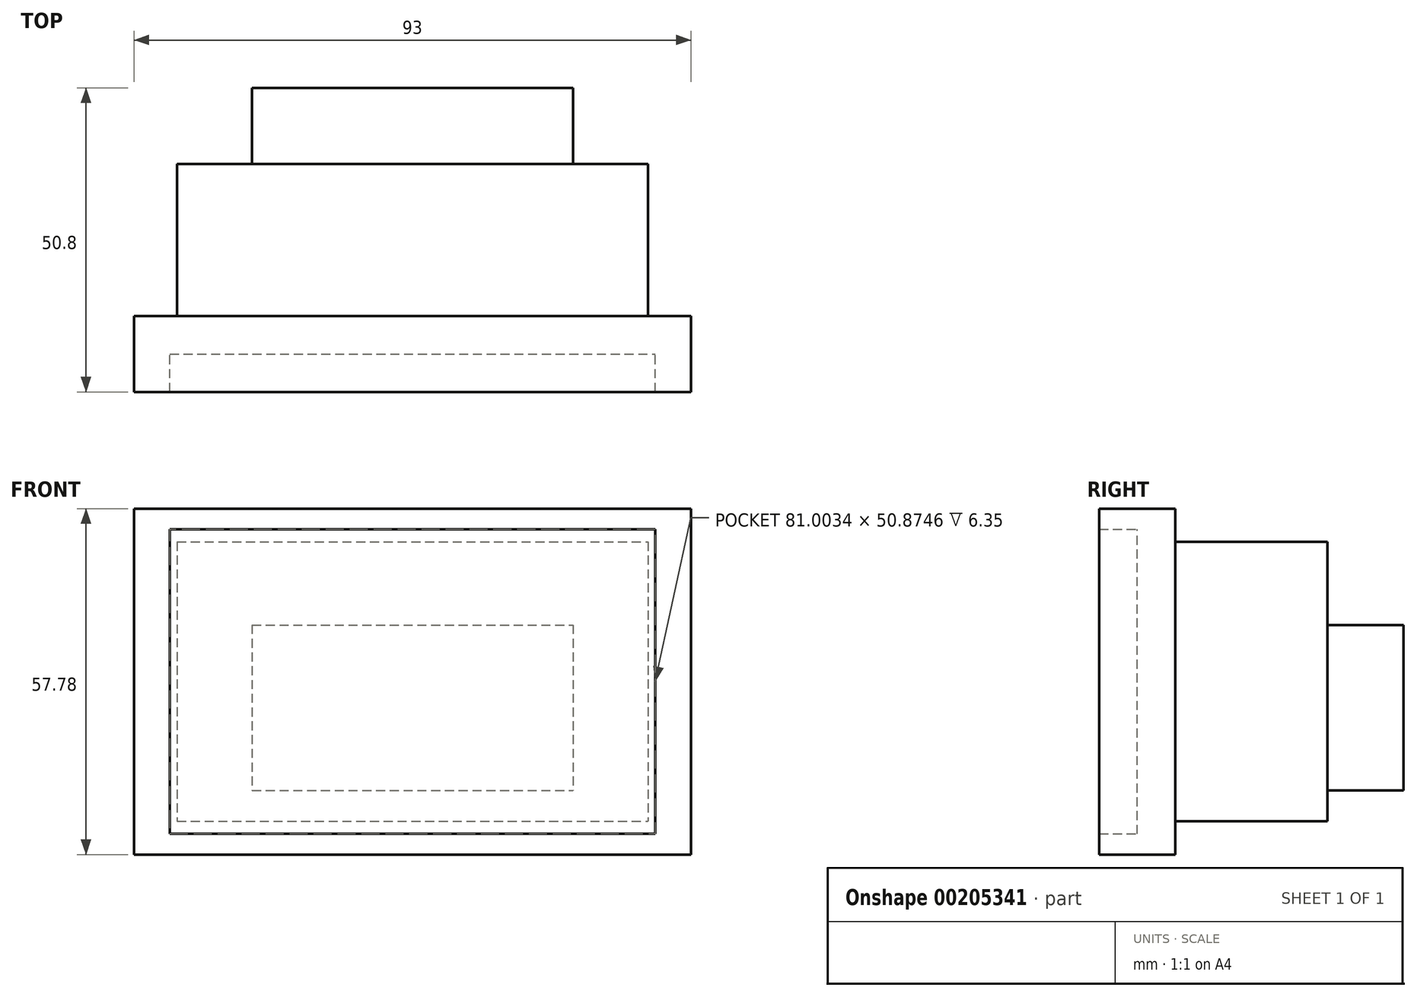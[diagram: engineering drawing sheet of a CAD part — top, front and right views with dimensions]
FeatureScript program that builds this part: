
annotation { "Feature Type Name" : "Feature", "Feature Type Description" : "" }
export const myFeature = defineFeature(function(context is Context, id is Id, definition is map)
    precondition{}
    {
        {
            var Q0;
            Q0=qCreatedBy(makeId("Front.planeOp"),FACE);
            var sketch = newSketch(context, id + "F0", { "sketchPlane" : qUnion([Q0])});
            skLineSegment(sketch, "E0.bottom", {"start": v(44.23, 29.1) * mm, "end": v(-44.23, 29.1) * mm});
            skLineSegment(sketch, "E0.top", {"start": v(44.23, -29.1) * mm, "end": v(-44.23, -29.1) * mm});
            skLineSegment(sketch, "E0.left", {"start": v(44.23, 29.1) * mm, "end": v(44.23, -29.1) * mm});
            skLineSegment(sketch, "E0.right", {"start": v(-44.23, 29.1) * mm, "end": v(-44.23, -29.1) * mm});
            skPoint(sketch, "E0.middle", {"position": v(0, 0) * mm});
            skLineSegment(sketch, "E1.bottom", {"start": v(40.81, 25.7) * mm, "end": v(-40.81, 25.7) * mm});
            skLineSegment(sketch, "E1.top", {"start": v(40.81, -25.7) * mm, "end": v(-40.81, -25.7) * mm});
            skLineSegment(sketch, "E1.left", {"start": v(40.81, 25.7) * mm, "end": v(40.81, -25.7) * mm});
            skLineSegment(sketch, "E1.right", {"start": v(-40.81, 25.7) * mm, "end": v(-40.81, -25.7) * mm});
            skSolve(sketch);
        }
        {
            var Q0;
            Q0=makeQuery(id+"F0.imprint","IMPRINT",FACE,{"disambiguationData":[TD([[makeQuery(id+"F0.imprint","IMPRINT",EDGE,{"derivedFrom":sQuery(id+"F0.wireOp",EDGE,"E1.bottom")}),1.0]])]});
            extrude(context, id + "F1", {"entities" : qUnion([Q0]), "depth" : 6.35 * mm});
        }
        {
            var Q0;
            Q0=qCreatedBy(makeId("Front.planeOp"),FACE);
            var sketch = newSketch(context, id + "F2", { "sketchPlane" : qUnion([Q0])});
            skLineSegment(sketch, "E2.bottom", {"start": v(46.5, 28.89) * mm, "end": v(-46.5, 28.89) * mm});
            skLineSegment(sketch, "E2.top", {"start": v(46.5, -28.89) * mm, "end": v(-46.5, -28.89) * mm});
            skLineSegment(sketch, "E2.left", {"start": v(46.5, 28.89) * mm, "end": v(46.5, -28.89) * mm});
            skLineSegment(sketch, "E2.right", {"start": v(-46.5, 28.89) * mm, "end": v(-46.5, -28.89) * mm});
            skPoint(sketch, "E2.middle", {"position": v(0, 0) * mm});
            skLineSegment(sketch, "E3.bottom", {"start": v(40.5, 25.44) * mm, "end": v(-40.5, 25.44) * mm});
            skLineSegment(sketch, "E3.top", {"start": v(40.5, -25.44) * mm, "end": v(-40.5, -25.44) * mm});
            skLineSegment(sketch, "E3.left", {"start": v(40.5, 25.44) * mm, "end": v(40.5, -25.44) * mm});
            skLineSegment(sketch, "E3.right", {"start": v(-40.5, 25.44) * mm, "end": v(-40.5, -25.44) * mm});
            skSolve(sketch);
        }
        {
            var Q0;
            Q0=makeQuery(id+"F2.imprint","IMPRINT",FACE,{"disambiguationData":[TD([[makeQuery(id+"F2.imprint","IMPRINT",EDGE,{"derivedFrom":sQuery(id+"F2.wireOp",EDGE,"E2.bottom")}),1.0]])]});
            extrude(context, id + "F3", {"entities" : qUnion([Q0]), "operationType" : NewBodyOperationType.ADD, "depth" : 12.7 * mm});
        }
        {
            var Q0;
            Q0=makeQuery(id+"F3.boolean.opBoolean","MERGE",FACE,{"derivedFrom":[makeQuery(id+"F1.opExtrude","CAP_FACE",FACE,{"disambiguationData":[OSD([sQuery(id+"F0.wireOp",EDGE,"E1.bottom"),sQuery(id+"F0.wireOp",EDGE,"E1.top"),sQuery(id+"F0.wireOp",EDGE,"E1.left"),sQuery(id+"F0.wireOp",EDGE,"E1.right")])],"isStart":true}),makeQuery(id+"F3.opExtrude","CAP_FACE",FACE,{"disambiguationData":[OSD([sQuery(id+"F2.wireOp",EDGE,"E2.bottom"),sQuery(id+"F2.wireOp",EDGE,"E2.top"),sQuery(id+"F2.wireOp",EDGE,"E2.left"),sQuery(id+"F2.wireOp",EDGE,"E2.right"),sQuery(id+"F2.wireOp",EDGE,"E3.bottom"),sQuery(id+"F2.wireOp",EDGE,"E3.top"),sQuery(id+"F2.wireOp",EDGE,"E3.left"),sQuery(id+"F2.wireOp",EDGE,"E3.right")])],"isStart":true})]});
            var sketch = newSketch(context, id + "F4", { "sketchPlane" : qUnion([Q0])});
            skLineSegment(sketch, "E4.bottom", {"start": v(39.29, 23.33) * mm, "end": v(-39.29, 23.33) * mm});
            skLineSegment(sketch, "E4.top", {"start": v(39.29, -23.33) * mm, "end": v(-39.29, -23.33) * mm});
            skLineSegment(sketch, "E4.left", {"start": v(39.29, 23.33) * mm, "end": v(39.29, -23.33) * mm});
            skLineSegment(sketch, "E4.right", {"start": v(-39.29, 23.33) * mm, "end": v(-39.29, -23.33) * mm});
            skPoint(sketch, "E4.middle", {"position": v(0, 0) * mm});
            skSolve(sketch);
        }
        {
            var Q0;
            Q0=makeQuery(id+"F4.imprint","IMPRINT",FACE,{"disambiguationData":[TD([[makeQuery(id+"F4.imprint","IMPRINT",EDGE,{"derivedFrom":sQuery(id+"F4.wireOp",EDGE,"E4.bottom")}),1.0]])]});
            extrude(context, id + "F5", {"entities" : qUnion([Q0]), "operationType" : NewBodyOperationType.ADD, "depth" : 25.4 * mm});
        }
        {
            var Q0;
            Q0=makeQuery(id+"F5.opExtrude","CAP_FACE",FACE,{"disambiguationData":[OSD([sQuery(id+"F4.wireOp",EDGE,"E4.bottom"),sQuery(id+"F4.wireOp",EDGE,"E4.top"),sQuery(id+"F4.wireOp",EDGE,"E4.left"),sQuery(id+"F4.wireOp",EDGE,"E4.right")])],"isStart":false});
            var sketch = newSketch(context, id + "F6", { "sketchPlane" : qUnion([Q0])});
            skLineSegment(sketch, "E5.bottom", {"start": v(26.78, 9.46) * mm, "end": v(-26.78, 9.46) * mm});
            skLineSegment(sketch, "E5.top", {"start": v(26.78, -18.21) * mm, "end": v(-26.78, -18.21) * mm});
            skLineSegment(sketch, "E5.left", {"start": v(26.78, 9.46) * mm, "end": v(26.78, -18.21) * mm});
            skLineSegment(sketch, "E5.right", {"start": v(-26.78, 9.46) * mm, "end": v(-26.78, -18.21) * mm});
            skPoint(sketch, "E5.middle", {"position": v(0, -4.38) * mm});
            skSolve(sketch);
        }
        {
            var Q0;
            Q0=makeQuery(id+"F6.imprint","IMPRINT",FACE,{"disambiguationData":[TD([[makeQuery(id+"F6.imprint","IMPRINT",EDGE,{"derivedFrom":sQuery(id+"F6.wireOp",EDGE,"E5.bottom")}),1.0]])]});
            extrude(context, id + "F7", {"entities" : qUnion([Q0]), "operationType" : NewBodyOperationType.ADD, "depth" : 12.7 * mm});
        }
    });
